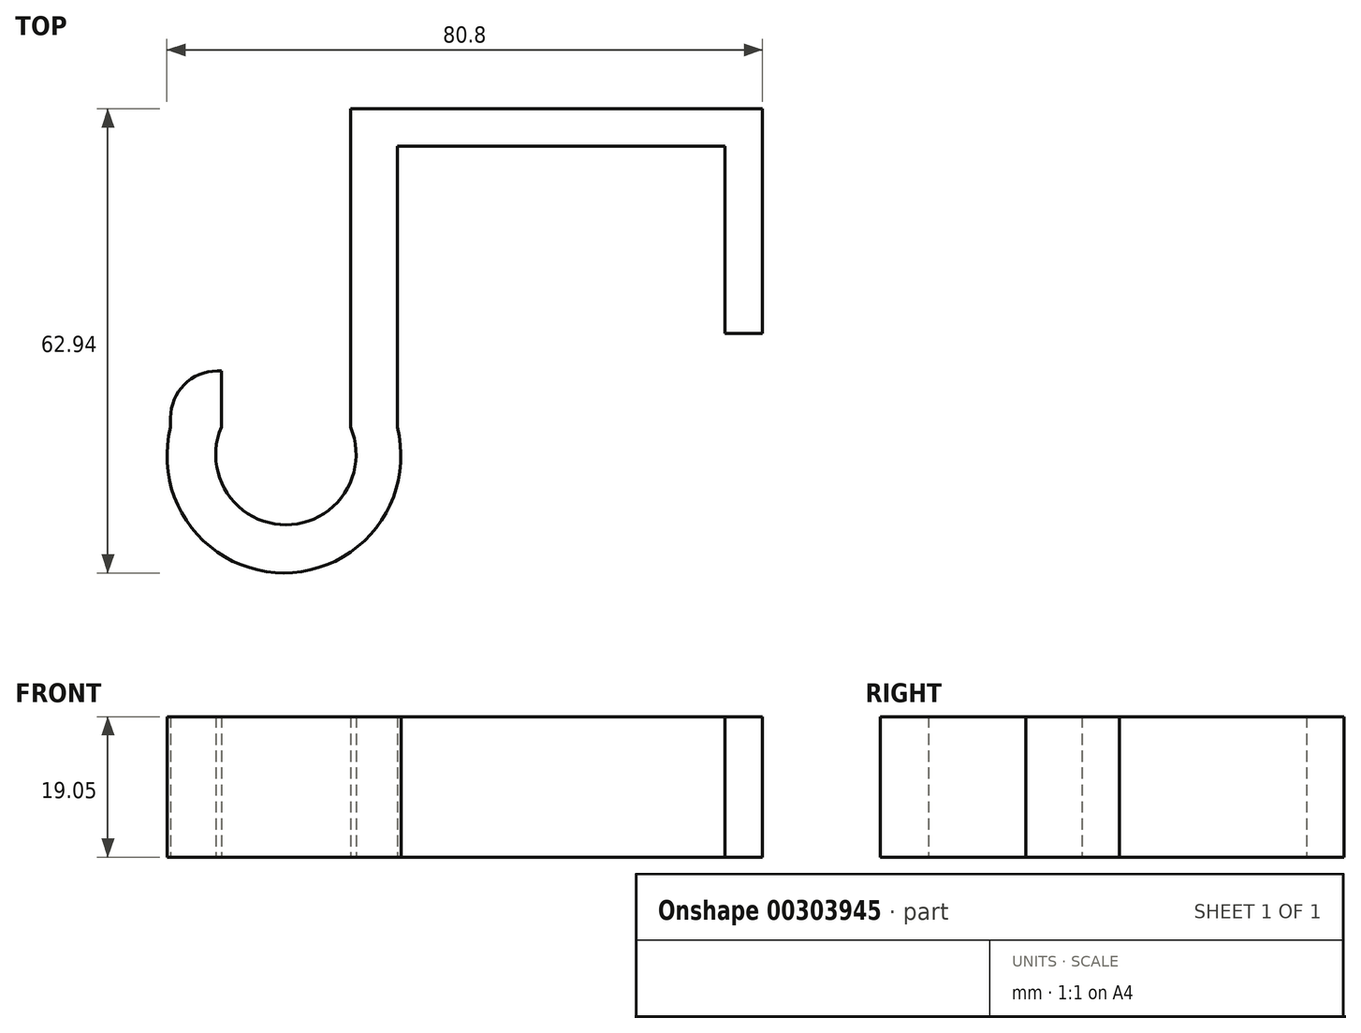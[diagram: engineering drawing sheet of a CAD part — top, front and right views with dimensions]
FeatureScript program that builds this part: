
annotation { "Feature Type Name" : "Feature", "Feature Type Description" : "" }
export const myFeature = defineFeature(function(context is Context, id is Id, definition is map)
    precondition{}
    {
        {
            var Q0;
            Q0=qCreatedBy(makeId("Top.planeOp"),FACE);
            var sketch = newSketch(context, id + "F0", { "sketchPlane" : qUnion([Q0])});
            skArc(sketch, "E0", {"start": v(-30.78, 0) * mm, "mid": v(-15.4, -19.76) * mm, "end": v(0, 0) * mm});
            skLineSegment(sketch, "E1", {"start": v(0, 0) * mm, "end": v(0, 38.1) * mm});
            skLineSegment(sketch, "E2", {"start": v(0, 38.1) * mm, "end": v(44.45, 38.1) * mm});
            skLineSegment(sketch, "E3", {"start": v(44.45, 38.1) * mm, "end": v(44.45, 12.7) * mm});
            skLineSegment(sketch, "E4", {"start": v(44.45, 12.7) * mm, "end": v(49.53, 12.7) * mm});
            skLineSegment(sketch, "E5", {"start": v(49.53, 12.7) * mm, "end": v(49.53, 43.18) * mm});
            skLineSegment(sketch, "E6", {"start": v(49.53, 43.18) * mm, "end": v(0, 43.18) * mm});
            skLineSegment(sketch, "E7", {"start": v(0, 43.18) * mm, "end": v(-6.35, 43.18) * mm});
            skLineSegment(sketch, "E8", {"start": v(-21.92, 3.05) * mm, "end": v(-21.92, 3.05) * mm});
            skLineSegment(sketch, "E9", {"start": v(-6.35, 43.18) * mm, "end": v(-6.35, 0) * mm});
            skArc(sketch, "E10", {"start": v(-23.9, 0) * mm, "mid": v(-15.13, -13.23) * mm, "end": v(-6.35, 0) * mm});
            skLineSegment(sketch, "E11", {"start": v(-23.9, 0) * mm, "end": v(-23.9, 7.62) * mm});
            skLineSegment(sketch, "E12", {"start": v(-30.78, 0) * mm, "end": v(-30.78, 1.27) * mm});
            skLineSegment(sketch, "E13", {"start": v(-24.43, 7.62) * mm, "end": v(-23.9, 7.62) * mm});
            skPoint(sketch, "E14.visualSharp", {"position": v(-30.78, 7.62) * mm});
            skArc(sketch, "E14.filletArc", {"start": v(-24.43, 7.62) * mm, "mid": v(-28.92, 5.76) * mm, "end": v(-30.78, 1.27) * mm});
            skSolve(sketch);
        }
        {
            var Q0;
            Q0=makeQuery(id+"F0.imprint","IMPRINT",FACE,{"disambiguationData":[TD([[makeQuery(id+"F0.imprint","IMPRINT",EDGE,{"derivedFrom":sQuery(id+"F0.wireOp",EDGE,"E0")}),1.0]])]});
            extrude(context, id + "F1", {"entities" : qUnion([Q0]), "depth" : 19.05 * mm});
        }
    });
